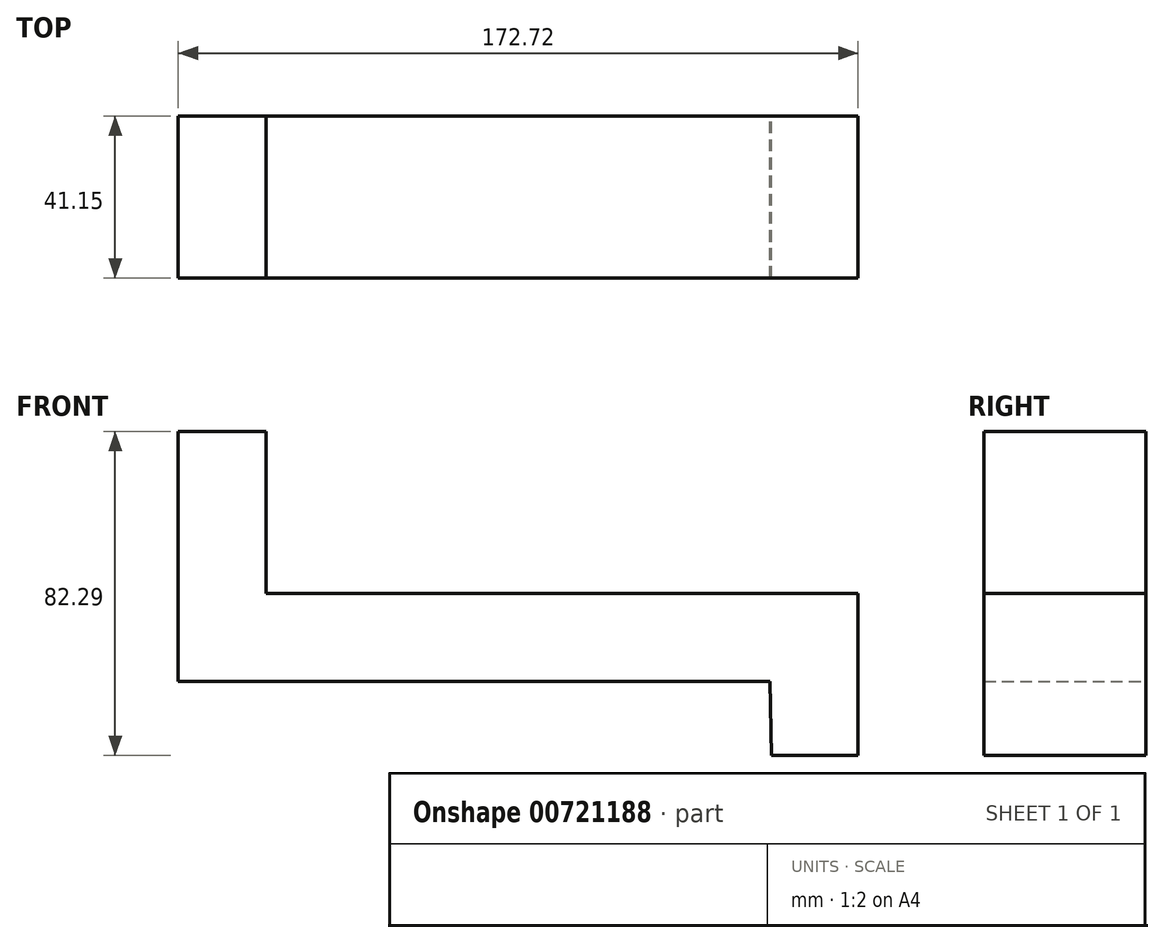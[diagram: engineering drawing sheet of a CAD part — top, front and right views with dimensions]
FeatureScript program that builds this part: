
annotation { "Feature Type Name" : "Feature", "Feature Type Description" : "" }
export const myFeature = defineFeature(function(context is Context, id is Id, definition is map)
    precondition{}
    {
        {
            var Q0;
            Q0=qCreatedBy(makeId("Front.planeOp"),FACE);
            var sketch = newSketch(context, id + "F0", { "sketchPlane" : qUnion([Q0])});
            skLineSegment(sketch, "E0", {"start": v(-172.72, 49.9) * mm, "end": v(-172.72, -13.6) * mm});
            skLineSegment(sketch, "E1", {"start": v(-172.72, 49.9) * mm, "end": v(-150.37, 49.9) * mm});
            skLineSegment(sketch, "E2", {"start": v(-150.37, 49.9) * mm, "end": v(-150.37, 8.75) * mm});
            skLineSegment(sketch, "E3", {"start": v(-172.72, -13.6) * mm, "end": v(-22.35, -13.6) * mm});
            skLineSegment(sketch, "E4", {"start": v(-150.37, 8.75) * mm, "end": v(0, 8.75) * mm});
            skLineSegment(sketch, "E5", {"start": v(0, 8.75) * mm, "end": v(0, -13.6) * mm});
            skLineSegment(sketch, "E6", {"start": v(0, -13.6) * mm, "end": v(0, -32.4) * mm});
            skLineSegment(sketch, "E7", {"start": v(0, -32.4) * mm, "end": v(-21.98, -32.4) * mm});
            skLineSegment(sketch, "E8", {"start": v(-21.98, -32.4) * mm, "end": v(-22.35, -13.6) * mm});
            skSolve(sketch);
        }
        {
            var Q0;
            Q0 = qSketchRegion(id + "F0", true);
            extrude(context, id + "F1", {"entities" : qUnion([Q0]), "depth" : 41.15 * mm, "offsetDistance" : 25.4 * mm});
        }
    });
